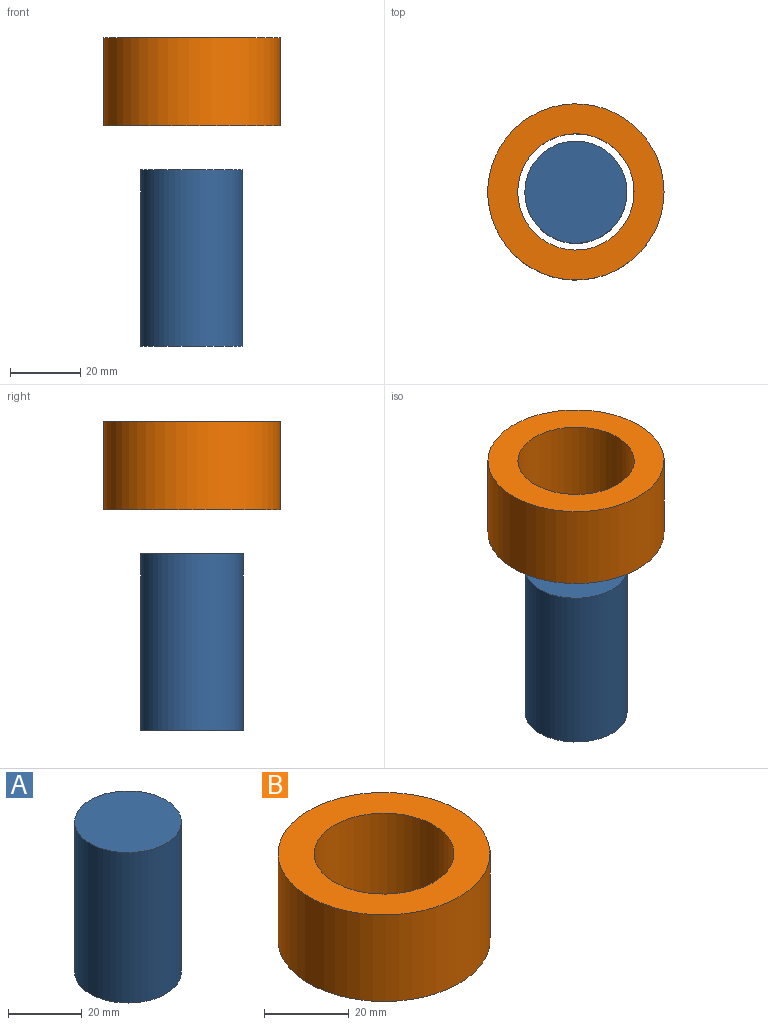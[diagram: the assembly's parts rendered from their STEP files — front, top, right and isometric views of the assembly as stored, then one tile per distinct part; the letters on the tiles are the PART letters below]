
ASSEMBLY  parts=2 mates=2
PART A: 3 faces, bbox 29x29x50 mm
  f0: cylinder r=14.5mm len=50mm, axis (0,0,-1), area 4555.3mm2, adj f1,f2
  f1: plane 29x29mm, normal (0,0,1), area 660.5mm2, adj f0
  f2: plane 29x29mm, normal (0,0,-1), area 660.5mm2, adj f0
PART B: 4 faces, bbox 50x50x25 mm
  f0: cylinder r=16.5mm len=33mm, axis (0,0,-1), area 2591.8mm2, adj f2,f3
  f1: cylinder r=25mm len=50mm, axis (0,0,-1), area 3927mm2, adj f2,f3
  f2: plane 50x50mm, normal (0,0,1), area 1108.2mm2, adj f0,f1
  f3: plane 50x50mm, normal (0,0,-1), area 1108.2mm2, adj f0,f1
PLACE A rot(axis=(0,0,1),180deg) t=(9.94,128.22,-49.4)mm
PLACE B rot(axis=(0,0,-1),0deg) t=(9.94,128.22,13.1)mm
MATE slider A.f0 <-> B.f1  axis (0,0,-1) through (9.94,128.22,-24.4)mm
MATE cylindrical B.f1 <-> A.f0  axis (0,0,1) through (9.94,128.22,38.1)mm
